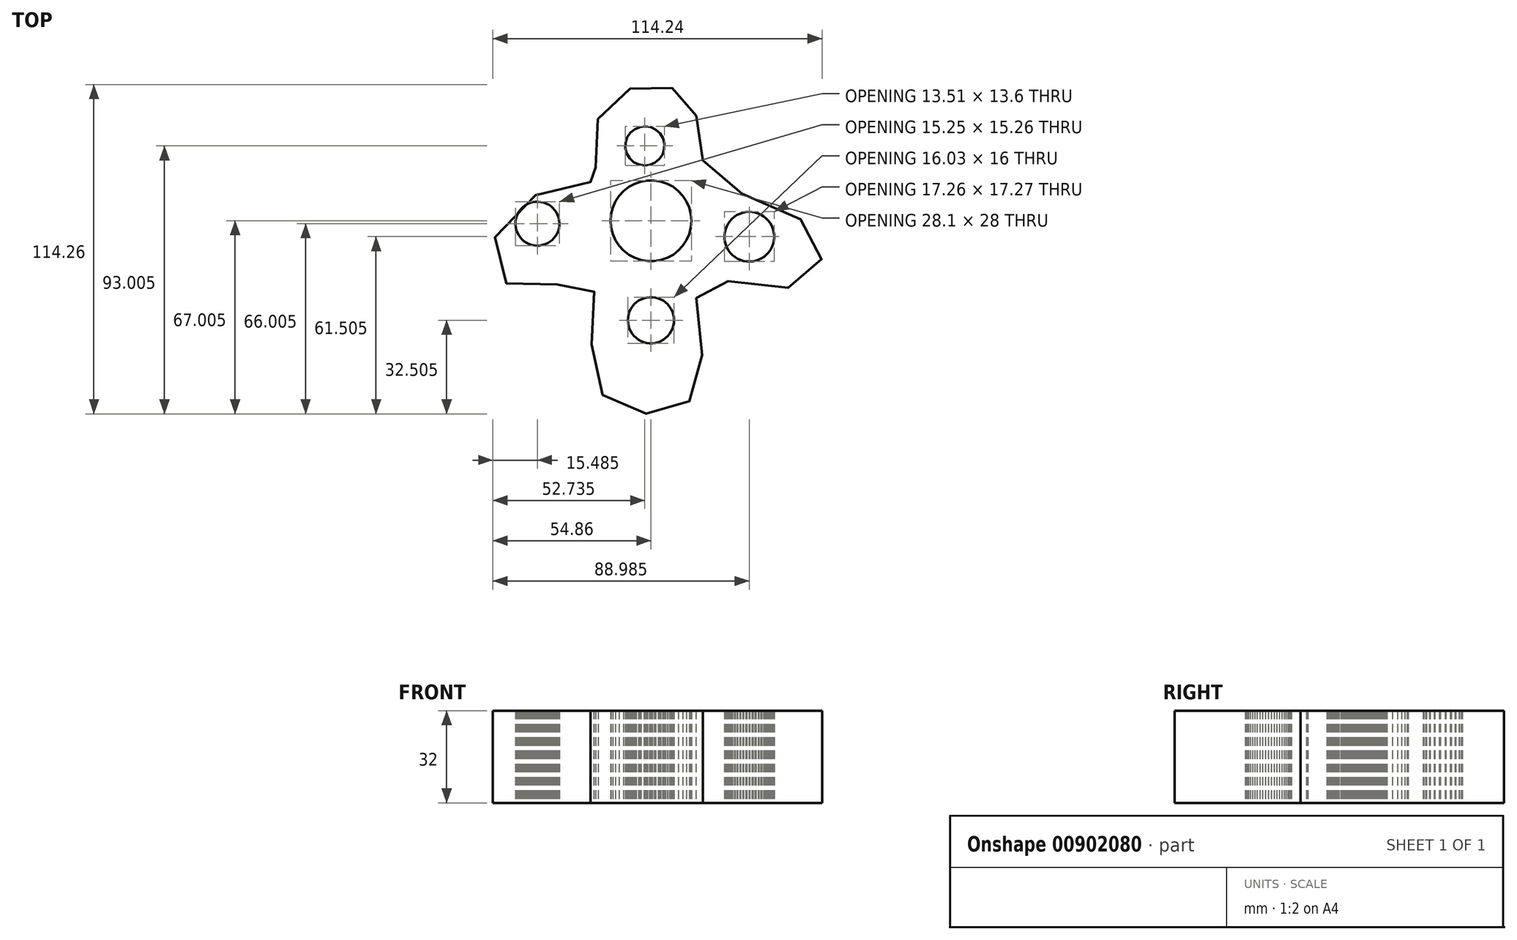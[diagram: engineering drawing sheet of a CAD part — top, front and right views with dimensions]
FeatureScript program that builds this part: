
annotation { "Feature Type Name" : "Feature", "Feature Type Description" : "" }
export const myFeature = defineFeature(function(context is Context, id is Id, definition is map)
    precondition{}
    {
        {
            var Q0;
            Q0=qCreatedBy(makeId("Top.planeOp"),FACE);
            var sketch = newSketch(context, id + "F0", { "sketchPlane" : qUnion([Q0])});
            skFitSpline(sketch, "E0", {"points": [v(-18.37, 57.62) * mm, v(-18.37, 36.88) * mm, v(-18.37, 36.38) * mm, v(-48.88, 25.88) * mm, v(-49.13, 0) * mm, v(-21.12, 0) * mm, v(-20.38, -31.13) * mm, v(0, -44.63) * mm, v(17.62, -32.63) * mm, v(17.62, 0) * mm, v(51.63, 0) * mm, v(57.13, 18.37) * mm, v(20.63, 38.63) * mm, v(14.87, 61.63) * mm, v(0, 69.62) * mm, v(-18.37, 57.62) * mm]});
            skCircle(sketch, "E1.cCircle", {"center": v(0, 22.38) * mm, "radius": 14 * mm, "construction": true});
            skLineSegment(sketch, "E1.0", {"start": v(1.16, 8.38) * mm, "end": v(-1.16, 8.38) * mm});
            skLineSegment(sketch, "E1.1", {"start": v(-1.16, 8.38) * mm, "end": v(-3.45, 8.76) * mm});
            skLineSegment(sketch, "E1.2", {"start": v(-3.45, 8.76) * mm, "end": v(-5.64, 9.51) * mm});
            skLineSegment(sketch, "E1.3", {"start": v(-5.64, 9.51) * mm, "end": v(-7.68, 10.61) * mm});
            skLineSegment(sketch, "E1.4", {"start": v(-7.68, 10.61) * mm, "end": v(-9.51, 12.04) * mm});
            skLineSegment(sketch, "E1.5", {"start": v(-9.51, 12.04) * mm, "end": v(-11.09, 13.75) * mm});
            skLineSegment(sketch, "E1.6", {"start": v(-11.09, 13.75) * mm, "end": v(-12.35, 15.69) * mm});
            skLineSegment(sketch, "E1.7", {"start": v(-12.35, 15.69) * mm, "end": v(-13.29, 17.81) * mm});
            skLineSegment(sketch, "E1.8", {"start": v(-13.29, 17.81) * mm, "end": v(-13.86, 20.06) * mm});
            skLineSegment(sketch, "E1.9", {"start": v(-13.86, 20.06) * mm, "end": v(-14.05, 22.38) * mm});
            skLineSegment(sketch, "E1.10", {"start": v(-14.05, 22.38) * mm, "end": v(-13.86, 24.69) * mm});
            skLineSegment(sketch, "E1.11", {"start": v(-13.86, 24.69) * mm, "end": v(-13.29, 26.94) * mm});
            skLineSegment(sketch, "E1.12", {"start": v(-13.29, 26.94) * mm, "end": v(-12.35, 29.06) * mm});
            skLineSegment(sketch, "E1.13", {"start": v(-12.35, 29.06) * mm, "end": v(-11.09, 31) * mm});
            skLineSegment(sketch, "E1.14", {"start": v(-11.09, 31) * mm, "end": v(-9.51, 32.71) * mm});
            skLineSegment(sketch, "E1.15", {"start": v(-9.51, 32.71) * mm, "end": v(-7.68, 34.14) * mm});
            skLineSegment(sketch, "E1.16", {"start": v(-7.68, 34.14) * mm, "end": v(-5.64, 35.24) * mm});
            skLineSegment(sketch, "E1.17", {"start": v(-5.64, 35.24) * mm, "end": v(-3.45, 36) * mm});
            skLineSegment(sketch, "E1.18", {"start": v(-3.45, 36) * mm, "end": v(-1.16, 36.38) * mm});
            skLineSegment(sketch, "E1.19", {"start": v(-1.16, 36.38) * mm, "end": v(1.16, 36.38) * mm});
            skLineSegment(sketch, "E1.20", {"start": v(1.16, 36.38) * mm, "end": v(3.45, 36) * mm});
            skLineSegment(sketch, "E1.21", {"start": v(3.45, 36) * mm, "end": v(5.64, 35.24) * mm});
            skLineSegment(sketch, "E1.22", {"start": v(5.64, 35.24) * mm, "end": v(7.68, 34.14) * mm});
            skLineSegment(sketch, "E1.23", {"start": v(7.68, 34.14) * mm, "end": v(9.51, 32.71) * mm});
            skLineSegment(sketch, "E1.24", {"start": v(9.51, 32.71) * mm, "end": v(11.09, 31) * mm});
            skLineSegment(sketch, "E1.25", {"start": v(11.09, 31) * mm, "end": v(12.35, 29.06) * mm});
            skLineSegment(sketch, "E1.26", {"start": v(12.35, 29.06) * mm, "end": v(13.29, 26.94) * mm});
            skLineSegment(sketch, "E1.27", {"start": v(13.29, 26.94) * mm, "end": v(13.86, 24.69) * mm});
            skLineSegment(sketch, "E1.28", {"start": v(13.86, 24.69) * mm, "end": v(14.05, 22.38) * mm});
            skLineSegment(sketch, "E1.29", {"start": v(14.05, 22.38) * mm, "end": v(13.86, 20.06) * mm});
            skLineSegment(sketch, "E1.30", {"start": v(13.86, 20.06) * mm, "end": v(13.29, 17.81) * mm});
            skLineSegment(sketch, "E1.31", {"start": v(13.29, 17.81) * mm, "end": v(12.35, 15.69) * mm});
            skLineSegment(sketch, "E1.32", {"start": v(12.35, 15.69) * mm, "end": v(11.09, 13.75) * mm});
            skLineSegment(sketch, "E1.33", {"start": v(11.09, 13.75) * mm, "end": v(9.51, 12.04) * mm});
            skLineSegment(sketch, "E1.34", {"start": v(9.51, 12.04) * mm, "end": v(7.68, 10.61) * mm});
            skLineSegment(sketch, "E1.35", {"start": v(7.68, 10.61) * mm, "end": v(5.64, 9.51) * mm});
            skLineSegment(sketch, "E1.36", {"start": v(5.64, 9.51) * mm, "end": v(3.45, 8.76) * mm});
            skLineSegment(sketch, "E1.37", {"start": v(3.45, 8.76) * mm, "end": v(1.16, 8.38) * mm});
            skPoint(sketch, "E1.0.midPoint", {"position": v(0, 8.38) * mm});
            skCircle(sketch, "E2.cCircle", {"center": v(34.13, 16.88) * mm, "radius": 8.62 * mm, "construction": true});
            skLineSegment(sketch, "E2.0", {"start": v(32.14, 8.47) * mm, "end": v(31.1, 8.78) * mm});
            skLineSegment(sketch, "E2.1", {"start": v(31.1, 8.78) * mm, "end": v(30.12, 9.22) * mm});
            skLineSegment(sketch, "E2.2", {"start": v(30.12, 9.22) * mm, "end": v(29.19, 9.79) * mm});
            skLineSegment(sketch, "E2.3", {"start": v(29.19, 9.79) * mm, "end": v(28.34, 10.46) * mm});
            skLineSegment(sketch, "E2.4", {"start": v(28.34, 10.46) * mm, "end": v(27.58, 11.24) * mm});
            skLineSegment(sketch, "E2.5", {"start": v(27.58, 11.24) * mm, "end": v(26.93, 12.1) * mm});
            skLineSegment(sketch, "E2.6", {"start": v(26.93, 12.1) * mm, "end": v(26.38, 13.04) * mm});
            skLineSegment(sketch, "E2.7", {"start": v(26.38, 13.04) * mm, "end": v(25.97, 14.04) * mm});
            skLineSegment(sketch, "E2.8", {"start": v(25.97, 14.04) * mm, "end": v(25.67, 15.09) * mm});
            skLineSegment(sketch, "E2.9", {"start": v(25.67, 15.09) * mm, "end": v(25.52, 16.16) * mm});
            skLineSegment(sketch, "E2.10", {"start": v(25.52, 16.16) * mm, "end": v(25.5, 17.25) * mm});
            skLineSegment(sketch, "E2.11", {"start": v(25.5, 17.25) * mm, "end": v(25.6, 18.32) * mm});
            skLineSegment(sketch, "E2.12", {"start": v(25.6, 18.32) * mm, "end": v(25.86, 19.38) * mm});
            skLineSegment(sketch, "E2.13", {"start": v(25.86, 19.38) * mm, "end": v(26.24, 20.4) * mm});
            skLineSegment(sketch, "E2.14", {"start": v(26.24, 20.4) * mm, "end": v(26.74, 21.36) * mm});
            skLineSegment(sketch, "E2.15", {"start": v(26.74, 21.36) * mm, "end": v(27.36, 22.25) * mm});
            skLineSegment(sketch, "E2.16", {"start": v(27.36, 22.25) * mm, "end": v(28.09, 23.05) * mm});
            skLineSegment(sketch, "E2.17", {"start": v(28.09, 23.05) * mm, "end": v(28.9, 23.76) * mm});
            skLineSegment(sketch, "E2.18", {"start": v(28.9, 23.76) * mm, "end": v(29.81, 24.36) * mm});
            skLineSegment(sketch, "E2.19", {"start": v(29.81, 24.36) * mm, "end": v(30.79, 24.84) * mm});
            skLineSegment(sketch, "E2.20", {"start": v(30.79, 24.84) * mm, "end": v(31.81, 25.2) * mm});
            skLineSegment(sketch, "E2.21", {"start": v(31.81, 25.2) * mm, "end": v(32.87, 25.42) * mm});
            skLineSegment(sketch, "E2.22", {"start": v(32.87, 25.42) * mm, "end": v(33.95, 25.51) * mm});
            skLineSegment(sketch, "E2.23", {"start": v(33.95, 25.51) * mm, "end": v(35.04, 25.46) * mm});
            skLineSegment(sketch, "E2.24", {"start": v(35.04, 25.46) * mm, "end": v(36.1, 25.28) * mm});
            skLineSegment(sketch, "E2.25", {"start": v(36.1, 25.28) * mm, "end": v(37.14, 24.97) * mm});
            skLineSegment(sketch, "E2.26", {"start": v(37.14, 24.97) * mm, "end": v(38.13, 24.53) * mm});
            skLineSegment(sketch, "E2.27", {"start": v(38.13, 24.53) * mm, "end": v(39.06, 23.96) * mm});
            skLineSegment(sketch, "E2.28", {"start": v(39.06, 23.96) * mm, "end": v(39.91, 23.29) * mm});
            skLineSegment(sketch, "E2.29", {"start": v(39.91, 23.29) * mm, "end": v(40.67, 22.51) * mm});
            skLineSegment(sketch, "E2.30", {"start": v(40.67, 22.51) * mm, "end": v(41.32, 21.65) * mm});
            skLineSegment(sketch, "E2.31", {"start": v(41.32, 21.65) * mm, "end": v(41.87, 20.7) * mm});
            skLineSegment(sketch, "E2.32", {"start": v(41.87, 20.7) * mm, "end": v(42.28, 19.7) * mm});
            skLineSegment(sketch, "E2.33", {"start": v(42.28, 19.7) * mm, "end": v(42.58, 18.66) * mm});
            skLineSegment(sketch, "E2.34", {"start": v(42.58, 18.66) * mm, "end": v(42.73, 17.59) * mm});
            skLineSegment(sketch, "E2.35", {"start": v(42.73, 17.59) * mm, "end": v(42.75, 16.5) * mm});
            skLineSegment(sketch, "E2.36", {"start": v(42.75, 16.5) * mm, "end": v(42.64, 15.43) * mm});
            skLineSegment(sketch, "E2.37", {"start": v(42.64, 15.43) * mm, "end": v(42.4, 14.37) * mm});
            skLineSegment(sketch, "E2.38", {"start": v(42.4, 14.37) * mm, "end": v(42.01, 13.35) * mm});
            skLineSegment(sketch, "E2.39", {"start": v(42.01, 13.35) * mm, "end": v(41.5, 12.4) * mm});
            skLineSegment(sketch, "E2.40", {"start": v(41.5, 12.4) * mm, "end": v(40.89, 11.5) * mm});
            skLineSegment(sketch, "E2.41", {"start": v(40.89, 11.5) * mm, "end": v(40.16, 10.7) * mm});
            skLineSegment(sketch, "E2.42", {"start": v(40.16, 10.7) * mm, "end": v(39.34, 9.99) * mm});
            skLineSegment(sketch, "E2.43", {"start": v(39.34, 9.99) * mm, "end": v(38.44, 9.4) * mm});
            skLineSegment(sketch, "E2.44", {"start": v(38.44, 9.4) * mm, "end": v(37.46, 8.9) * mm});
            skLineSegment(sketch, "E2.45", {"start": v(37.46, 8.9) * mm, "end": v(36.44, 8.55) * mm});
            skLineSegment(sketch, "E2.46", {"start": v(36.44, 8.55) * mm, "end": v(35.38, 8.33) * mm});
            skLineSegment(sketch, "E2.47", {"start": v(35.38, 8.33) * mm, "end": v(34.3, 8.24) * mm});
            skLineSegment(sketch, "E2.48", {"start": v(34.3, 8.24) * mm, "end": v(33.21, 8.29) * mm});
            skLineSegment(sketch, "E2.49", {"start": v(33.21, 8.29) * mm, "end": v(32.14, 8.47) * mm});
            skPoint(sketch, "E2.0.midPoint", {"position": v(31.63, 8.63) * mm});
            skCircle(sketch, "E3.cCircle", {"center": v(0, -12.13) * mm, "radius": 8 * mm, "construction": true});
            skLineSegment(sketch, "E3.0", {"start": v(0.5, -20.13) * mm, "end": v(-0.5, -20.13) * mm});
            skLineSegment(sketch, "E3.1", {"start": v(-0.5, -20.13) * mm, "end": v(-1.5, -20) * mm});
            skLineSegment(sketch, "E3.2", {"start": v(-1.5, -20) * mm, "end": v(-2.48, -19.75) * mm});
            skLineSegment(sketch, "E3.3", {"start": v(-2.48, -19.75) * mm, "end": v(-3.41, -19.38) * mm});
            skLineSegment(sketch, "E3.4", {"start": v(-3.41, -19.38) * mm, "end": v(-4.3, -18.9) * mm});
            skLineSegment(sketch, "E3.5", {"start": v(-4.3, -18.9) * mm, "end": v(-5.1, -18.3) * mm});
            skLineSegment(sketch, "E3.6", {"start": v(-5.1, -18.3) * mm, "end": v(-5.84, -17.61) * mm});
            skLineSegment(sketch, "E3.7", {"start": v(-5.84, -17.61) * mm, "end": v(-6.48, -16.84) * mm});
            skLineSegment(sketch, "E3.8", {"start": v(-6.48, -16.84) * mm, "end": v(-7.02, -15.99) * mm});
            skLineSegment(sketch, "E3.9", {"start": v(-7.02, -15.99) * mm, "end": v(-7.45, -15.08) * mm});
            skLineSegment(sketch, "E3.10", {"start": v(-7.45, -15.08) * mm, "end": v(-7.76, -14.12) * mm});
            skLineSegment(sketch, "E3.11", {"start": v(-7.76, -14.12) * mm, "end": v(-7.95, -13.13) * mm});
            skLineSegment(sketch, "E3.12", {"start": v(-7.95, -13.13) * mm, "end": v(-8.02, -12.13) * mm});
            skLineSegment(sketch, "E3.13", {"start": v(-8.02, -12.13) * mm, "end": v(-7.95, -11.12) * mm});
            skLineSegment(sketch, "E3.14", {"start": v(-7.95, -11.12) * mm, "end": v(-7.76, -10.13) * mm});
            skLineSegment(sketch, "E3.15", {"start": v(-7.76, -10.13) * mm, "end": v(-7.45, -9.17) * mm});
            skLineSegment(sketch, "E3.16", {"start": v(-7.45, -9.17) * mm, "end": v(-7.02, -8.26) * mm});
            skLineSegment(sketch, "E3.17", {"start": v(-7.02, -8.26) * mm, "end": v(-6.48, -7.41) * mm});
            skLineSegment(sketch, "E3.18", {"start": v(-6.48, -7.41) * mm, "end": v(-5.84, -6.64) * mm});
            skLineSegment(sketch, "E3.19", {"start": v(-5.84, -6.64) * mm, "end": v(-5.1, -5.95) * mm});
            skLineSegment(sketch, "E3.20", {"start": v(-5.1, -5.95) * mm, "end": v(-4.3, -5.36) * mm});
            skLineSegment(sketch, "E3.21", {"start": v(-4.3, -5.36) * mm, "end": v(-3.41, -4.87) * mm});
            skLineSegment(sketch, "E3.22", {"start": v(-3.41, -4.87) * mm, "end": v(-2.48, -4.5) * mm});
            skLineSegment(sketch, "E3.23", {"start": v(-2.48, -4.5) * mm, "end": v(-1.5, -4.25) * mm});
            skLineSegment(sketch, "E3.24", {"start": v(-1.5, -4.25) * mm, "end": v(-0.5, -4.13) * mm});
            skLineSegment(sketch, "E3.25", {"start": v(-0.5, -4.13) * mm, "end": v(0.5, -4.13) * mm});
            skLineSegment(sketch, "E3.26", {"start": v(0.5, -4.13) * mm, "end": v(1.5, -4.25) * mm});
            skLineSegment(sketch, "E3.27", {"start": v(1.5, -4.25) * mm, "end": v(2.48, -4.5) * mm});
            skLineSegment(sketch, "E3.28", {"start": v(2.48, -4.5) * mm, "end": v(3.41, -4.87) * mm});
            skLineSegment(sketch, "E3.29", {"start": v(3.41, -4.87) * mm, "end": v(4.3, -5.36) * mm});
            skLineSegment(sketch, "E3.30", {"start": v(4.3, -5.36) * mm, "end": v(5.1, -5.95) * mm});
            skLineSegment(sketch, "E3.31", {"start": v(5.1, -5.95) * mm, "end": v(5.84, -6.64) * mm});
            skLineSegment(sketch, "E3.32", {"start": v(5.84, -6.64) * mm, "end": v(6.48, -7.41) * mm});
            skLineSegment(sketch, "E3.33", {"start": v(6.48, -7.41) * mm, "end": v(7.02, -8.26) * mm});
            skLineSegment(sketch, "E3.34", {"start": v(7.02, -8.26) * mm, "end": v(7.45, -9.17) * mm});
            skLineSegment(sketch, "E3.35", {"start": v(7.45, -9.17) * mm, "end": v(7.76, -10.13) * mm});
            skLineSegment(sketch, "E3.36", {"start": v(7.76, -10.13) * mm, "end": v(7.95, -11.12) * mm});
            skLineSegment(sketch, "E3.37", {"start": v(7.95, -11.12) * mm, "end": v(8.02, -12.13) * mm});
            skLineSegment(sketch, "E3.38", {"start": v(8.02, -12.13) * mm, "end": v(7.95, -13.13) * mm});
            skLineSegment(sketch, "E3.39", {"start": v(7.95, -13.13) * mm, "end": v(7.76, -14.12) * mm});
            skLineSegment(sketch, "E3.40", {"start": v(7.76, -14.12) * mm, "end": v(7.45, -15.08) * mm});
            skLineSegment(sketch, "E3.41", {"start": v(7.45, -15.08) * mm, "end": v(7.02, -15.99) * mm});
            skLineSegment(sketch, "E3.42", {"start": v(7.02, -15.99) * mm, "end": v(6.48, -16.84) * mm});
            skLineSegment(sketch, "E3.43", {"start": v(6.48, -16.84) * mm, "end": v(5.84, -17.61) * mm});
            skLineSegment(sketch, "E3.44", {"start": v(5.84, -17.61) * mm, "end": v(5.1, -18.3) * mm});
            skLineSegment(sketch, "E3.45", {"start": v(5.1, -18.3) * mm, "end": v(4.3, -18.9) * mm});
            skLineSegment(sketch, "E3.46", {"start": v(4.3, -18.9) * mm, "end": v(3.41, -19.38) * mm});
            skLineSegment(sketch, "E3.47", {"start": v(3.41, -19.38) * mm, "end": v(2.48, -19.75) * mm});
            skLineSegment(sketch, "E3.48", {"start": v(2.48, -19.75) * mm, "end": v(1.5, -20) * mm});
            skLineSegment(sketch, "E3.49", {"start": v(1.5, -20) * mm, "end": v(0.5, -20.13) * mm});
            skPoint(sketch, "E3.0.midPoint", {"position": v(0, -20.13) * mm});
            skCircle(sketch, "E4.cCircle", {"center": v(-39.37, 21.38) * mm, "radius": 7.62 * mm, "construction": true});
            skLineSegment(sketch, "E4.0", {"start": v(-32.19, 18.82) * mm, "end": v(-32.56, 17.93) * mm});
            skLineSegment(sketch, "E4.1", {"start": v(-32.56, 17.93) * mm, "end": v(-33.05, 17.1) * mm});
            skLineSegment(sketch, "E4.2", {"start": v(-33.05, 17.1) * mm, "end": v(-33.63, 16.35) * mm});
            skLineSegment(sketch, "E4.3", {"start": v(-33.63, 16.35) * mm, "end": v(-34.3, 15.67) * mm});
            skLineSegment(sketch, "E4.4", {"start": v(-34.3, 15.67) * mm, "end": v(-35.06, 15.08) * mm});
            skLineSegment(sketch, "E4.5", {"start": v(-35.06, 15.08) * mm, "end": v(-35.89, 14.59) * mm});
            skLineSegment(sketch, "E4.6", {"start": v(-35.89, 14.59) * mm, "end": v(-36.76, 14.2) * mm});
            skLineSegment(sketch, "E4.7", {"start": v(-36.76, 14.2) * mm, "end": v(-37.68, 13.93) * mm});
            skLineSegment(sketch, "E4.8", {"start": v(-37.68, 13.93) * mm, "end": v(-38.63, 13.78) * mm});
            skLineSegment(sketch, "E4.9", {"start": v(-38.63, 13.78) * mm, "end": v(-39.59, 13.75) * mm});
            skLineSegment(sketch, "E4.10", {"start": v(-39.59, 13.75) * mm, "end": v(-40.54, 13.83) * mm});
            skLineSegment(sketch, "E4.11", {"start": v(-40.54, 13.83) * mm, "end": v(-41.48, 14.04) * mm});
            skLineSegment(sketch, "E4.12", {"start": v(-41.48, 14.04) * mm, "end": v(-42.38, 14.36) * mm});
            skLineSegment(sketch, "E4.13", {"start": v(-42.38, 14.36) * mm, "end": v(-43.24, 14.8) * mm});
            skLineSegment(sketch, "E4.14", {"start": v(-43.24, 14.8) * mm, "end": v(-44.03, 15.33) * mm});
            skLineSegment(sketch, "E4.15", {"start": v(-44.03, 15.33) * mm, "end": v(-44.75, 15.96) * mm});
            skLineSegment(sketch, "E4.16", {"start": v(-44.75, 15.96) * mm, "end": v(-45.39, 16.68) * mm});
            skLineSegment(sketch, "E4.17", {"start": v(-45.39, 16.68) * mm, "end": v(-45.93, 17.47) * mm});
            skLineSegment(sketch, "E4.18", {"start": v(-45.93, 17.47) * mm, "end": v(-46.37, 18.32) * mm});
            skLineSegment(sketch, "E4.19", {"start": v(-46.37, 18.32) * mm, "end": v(-46.7, 19.22) * mm});
            skLineSegment(sketch, "E4.20", {"start": v(-46.7, 19.22) * mm, "end": v(-46.9, 20.15) * mm});
            skLineSegment(sketch, "E4.21", {"start": v(-46.9, 20.15) * mm, "end": v(-47, 21.1) * mm});
            skLineSegment(sketch, "E4.22", {"start": v(-47, 21.1) * mm, "end": v(-46.97, 22.07) * mm});
            skLineSegment(sketch, "E4.23", {"start": v(-46.97, 22.07) * mm, "end": v(-46.83, 23.01) * mm});
            skLineSegment(sketch, "E4.24", {"start": v(-46.83, 23.01) * mm, "end": v(-46.56, 23.93) * mm});
            skLineSegment(sketch, "E4.25", {"start": v(-46.56, 23.93) * mm, "end": v(-46.19, 24.82) * mm});
            skLineSegment(sketch, "E4.26", {"start": v(-46.19, 24.82) * mm, "end": v(-45.7, 25.64) * mm});
            skLineSegment(sketch, "E4.27", {"start": v(-45.7, 25.64) * mm, "end": v(-45.12, 26.4) * mm});
            skLineSegment(sketch, "E4.28", {"start": v(-45.12, 26.4) * mm, "end": v(-44.44, 27.08) * mm});
            skLineSegment(sketch, "E4.29", {"start": v(-44.44, 27.08) * mm, "end": v(-43.69, 27.67) * mm});
            skLineSegment(sketch, "E4.30", {"start": v(-43.69, 27.67) * mm, "end": v(-42.86, 28.16) * mm});
            skLineSegment(sketch, "E4.31", {"start": v(-42.86, 28.16) * mm, "end": v(-41.99, 28.55) * mm});
            skLineSegment(sketch, "E4.32", {"start": v(-41.99, 28.55) * mm, "end": v(-41.07, 28.82) * mm});
            skLineSegment(sketch, "E4.33", {"start": v(-41.07, 28.82) * mm, "end": v(-40.12, 28.97) * mm});
            skLineSegment(sketch, "E4.34", {"start": v(-40.12, 28.97) * mm, "end": v(-39.16, 29) * mm});
            skLineSegment(sketch, "E4.35", {"start": v(-39.16, 29) * mm, "end": v(-38.2, 28.92) * mm});
            skLineSegment(sketch, "E4.36", {"start": v(-38.2, 28.92) * mm, "end": v(-37.27, 28.71) * mm});
            skLineSegment(sketch, "E4.37", {"start": v(-37.27, 28.71) * mm, "end": v(-36.37, 28.39) * mm});
            skLineSegment(sketch, "E4.38", {"start": v(-36.37, 28.39) * mm, "end": v(-35.51, 27.96) * mm});
            skLineSegment(sketch, "E4.39", {"start": v(-35.51, 27.96) * mm, "end": v(-34.72, 27.42) * mm});
            skLineSegment(sketch, "E4.40", {"start": v(-34.72, 27.42) * mm, "end": v(-34, 26.79) * mm});
            skLineSegment(sketch, "E4.41", {"start": v(-34, 26.79) * mm, "end": v(-33.36, 26.07) * mm});
            skLineSegment(sketch, "E4.42", {"start": v(-33.36, 26.07) * mm, "end": v(-32.82, 25.28) * mm});
            skLineSegment(sketch, "E4.43", {"start": v(-32.82, 25.28) * mm, "end": v(-32.38, 24.43) * mm});
            skLineSegment(sketch, "E4.44", {"start": v(-32.38, 24.43) * mm, "end": v(-32.05, 23.53) * mm});
            skLineSegment(sketch, "E4.45", {"start": v(-32.05, 23.53) * mm, "end": v(-31.84, 22.6) * mm});
            skLineSegment(sketch, "E4.46", {"start": v(-31.84, 22.6) * mm, "end": v(-31.75, 21.64) * mm});
            skLineSegment(sketch, "E4.47", {"start": v(-31.75, 21.64) * mm, "end": v(-31.78, 20.68) * mm});
            skLineSegment(sketch, "E4.48", {"start": v(-31.78, 20.68) * mm, "end": v(-31.92, 19.74) * mm});
            skLineSegment(sketch, "E4.49", {"start": v(-31.92, 19.74) * mm, "end": v(-32.19, 18.82) * mm});
            skPoint(sketch, "E4.0.midPoint", {"position": v(-32.38, 18.37) * mm});
            skCircle(sketch, "E5.cCircle", {"center": v(-2.13, 48.38) * mm, "radius": 6.73 * mm, "construction": true});
            skLineSegment(sketch, "E5.0", {"start": v(3.12, 52.7) * mm, "end": v(4.13, 51.05) * mm});
            skLineSegment(sketch, "E5.1", {"start": v(4.13, 51.05) * mm, "end": v(4.63, 49.18) * mm});
            skLineSegment(sketch, "E5.2", {"start": v(4.63, 49.18) * mm, "end": v(4.58, 47.24) * mm});
            skLineSegment(sketch, "E5.3", {"start": v(4.58, 47.24) * mm, "end": v(4, 45.4) * mm});
            skLineSegment(sketch, "E5.4", {"start": v(4, 45.4) * mm, "end": v(2.9, 43.8) * mm});
            skLineSegment(sketch, "E5.5", {"start": v(2.9, 43.8) * mm, "end": v(1.41, 42.57) * mm});
            skLineSegment(sketch, "E5.6", {"start": v(1.41, 42.57) * mm, "end": v(-0.37, 41.8) * mm});
            skLineSegment(sketch, "E5.7", {"start": v(-0.37, 41.8) * mm, "end": v(-2.3, 41.58) * mm});
            skLineSegment(sketch, "E5.8", {"start": v(-2.3, 41.58) * mm, "end": v(-4.2, 41.9) * mm});
            skLineSegment(sketch, "E5.9", {"start": v(-4.2, 41.9) * mm, "end": v(-5.94, 42.75) * mm});
            skLineSegment(sketch, "E5.10", {"start": v(-5.94, 42.75) * mm, "end": v(-7.37, 44.05) * mm});
            skLineSegment(sketch, "E5.11", {"start": v(-7.37, 44.05) * mm, "end": v(-8.38, 45.7) * mm});
            skLineSegment(sketch, "E5.12", {"start": v(-8.38, 45.7) * mm, "end": v(-8.88, 47.57) * mm});
            skLineSegment(sketch, "E5.13", {"start": v(-8.88, 47.57) * mm, "end": v(-8.83, 49.5) * mm});
            skLineSegment(sketch, "E5.14", {"start": v(-8.83, 49.5) * mm, "end": v(-8.24, 51.35) * mm});
            skLineSegment(sketch, "E5.15", {"start": v(-8.24, 51.35) * mm, "end": v(-7.15, 52.95) * mm});
            skLineSegment(sketch, "E5.16", {"start": v(-7.15, 52.95) * mm, "end": v(-5.66, 54.18) * mm});
            skLineSegment(sketch, "E5.17", {"start": v(-5.66, 54.18) * mm, "end": v(-3.88, 54.95) * mm});
            skLineSegment(sketch, "E5.18", {"start": v(-3.88, 54.95) * mm, "end": v(-1.96, 55.17) * mm});
            skLineSegment(sketch, "E5.19", {"start": v(-1.96, 55.17) * mm, "end": v(-0.05, 54.85) * mm});
            skLineSegment(sketch, "E5.20", {"start": v(-0.05, 54.85) * mm, "end": v(1.7, 54) * mm});
            skLineSegment(sketch, "E5.21", {"start": v(1.7, 54) * mm, "end": v(3.12, 52.7) * mm});
            skPoint(sketch, "E5.0.midPoint", {"position": v(3.63, 51.88) * mm});
            skSolve(sketch);
        }
        {
            var Q0;
            Q0 = qSketchRegion(id + "F0", true);
            var Q1;
            Q1=makeQuery(id+"F0.imprint","IMPRINT",FACE,{"disambiguationData":[TD([[makeQuery(id+"F0.imprint","IMPRINT",EDGE,{"derivedFrom":sQuery(id+"F0.wireOp",EDGE,"E0")}),1.0]])]});
            extrude(context, id + "F1", {"entities" : qUnion([Q0, Q1]), "depth" : 32 * mm, "offsetDistance" : 25 * mm});
        }
    });
